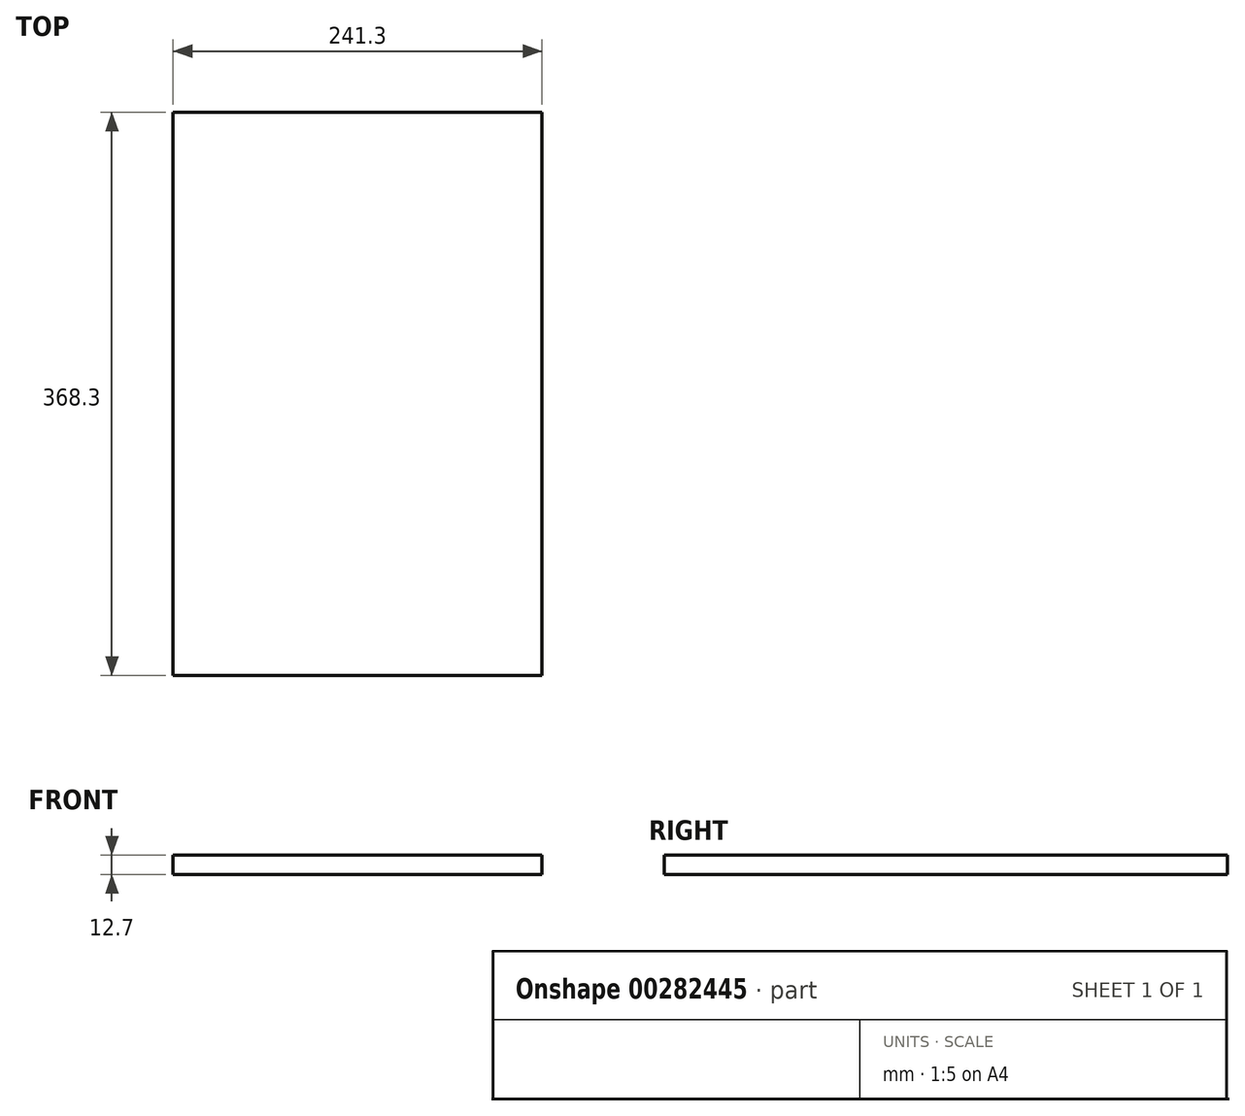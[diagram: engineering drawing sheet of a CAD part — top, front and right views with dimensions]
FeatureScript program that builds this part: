
annotation { "Feature Type Name" : "Feature", "Feature Type Description" : "" }
export const myFeature = defineFeature(function(context is Context, id is Id, definition is map)
    precondition{}
    {
        {
            var Q0;
            Q0=qCreatedBy(makeId("Top.planeOp"),FACE);
            var sketch = newSketch(context, id + "F0", { "sketchPlane" : qUnion([Q0])});
            skLineSegment(sketch, "E0.bottom", {"start": v(-103.81, 316.1) * mm, "end": v(137.49, 316.1) * mm});
            skLineSegment(sketch, "E0.top", {"start": v(-103.81, -52.2) * mm, "end": v(137.49, -52.2) * mm});
            skLineSegment(sketch, "E0.left", {"start": v(-103.81, 316.1) * mm, "end": v(-103.81, -52.2) * mm});
            skLineSegment(sketch, "E0.right", {"start": v(137.49, 316.1) * mm, "end": v(137.49, -52.2) * mm});
            skSolve(sketch);
        }
        {
            var Q0;
            Q0=makeQuery(id+"F0.imprint","IMPRINT",FACE,{"disambiguationData":[TD([[makeQuery(id+"F0.imprint","IMPRINT",EDGE,{"derivedFrom":sQuery(id+"F0.wireOp",EDGE,"E0.bottom")}),-1.0]])]});
            extrude(context, id + "F1", {"entities" : qUnion([Q0]), "depth" : 12.7 * mm});
        }
    });
